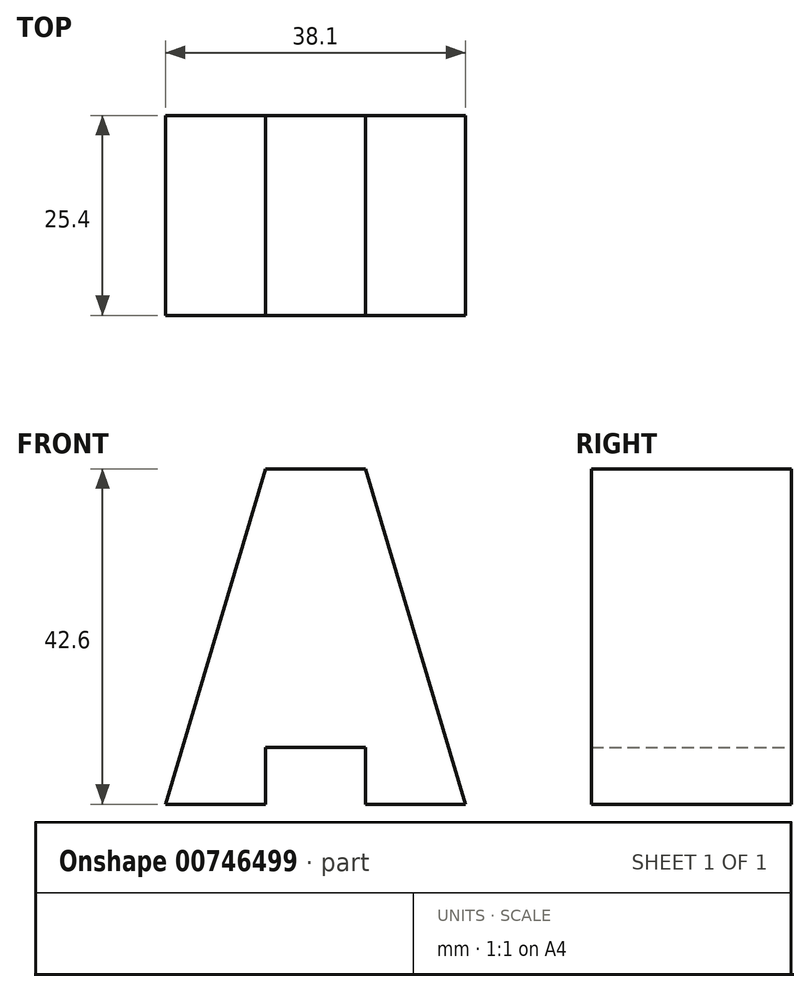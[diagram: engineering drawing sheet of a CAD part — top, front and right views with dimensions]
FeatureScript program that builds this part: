
annotation { "Feature Type Name" : "Feature", "Feature Type Description" : "" }
export const myFeature = defineFeature(function(context is Context, id is Id, definition is map)
    precondition{}
    {
        {
            var Q0;
            Q0=qCreatedBy(makeId("Front.planeOp"),FACE);
            var sketch = newSketch(context, id + "F0", { "sketchPlane" : qUnion([Q0])});
            skLineSegment(sketch, "E0", {"start": v(0, 0) * mm, "end": v(12.7, 0) * mm});
            skLineSegment(sketch, "E1", {"start": v(12.7, 0) * mm, "end": v(12.7, 7.2) * mm});
            skLineSegment(sketch, "E2", {"start": v(12.7, 7.2) * mm, "end": v(25.4, 7.2) * mm});
            skLineSegment(sketch, "E3", {"start": v(25.4, 7.2) * mm, "end": v(25.4, 0) * mm});
            skLineSegment(sketch, "E4", {"start": v(25.4, 0) * mm, "end": v(38.1, 0) * mm});
            skLineSegment(sketch, "E5", {"start": v(38.1, 0) * mm, "end": v(25.4, 42.6) * mm});
            skLineSegment(sketch, "E6", {"start": v(25.4, 42.6) * mm, "end": v(12.7, 42.6) * mm});
            skLineSegment(sketch, "E7", {"start": v(12.7, 42.6) * mm, "end": v(0, 0) * mm});
            skSolve(sketch);
        }
        {
            var Q0;
            Q0=makeQuery(id+"F0.imprint","IMPRINT",FACE,{"disambiguationData":[TD([[makeQuery(id+"F0.imprint","IMPRINT",EDGE,{"derivedFrom":sQuery(id+"F0.wireOp",EDGE,"E0")}),1.0]])]});
            extrude(context, id + "F1", {"entities" : qUnion([Q0]), "depth" : 25.4 * mm, "offsetDistance" : 25.4 * mm});
        }
    });
